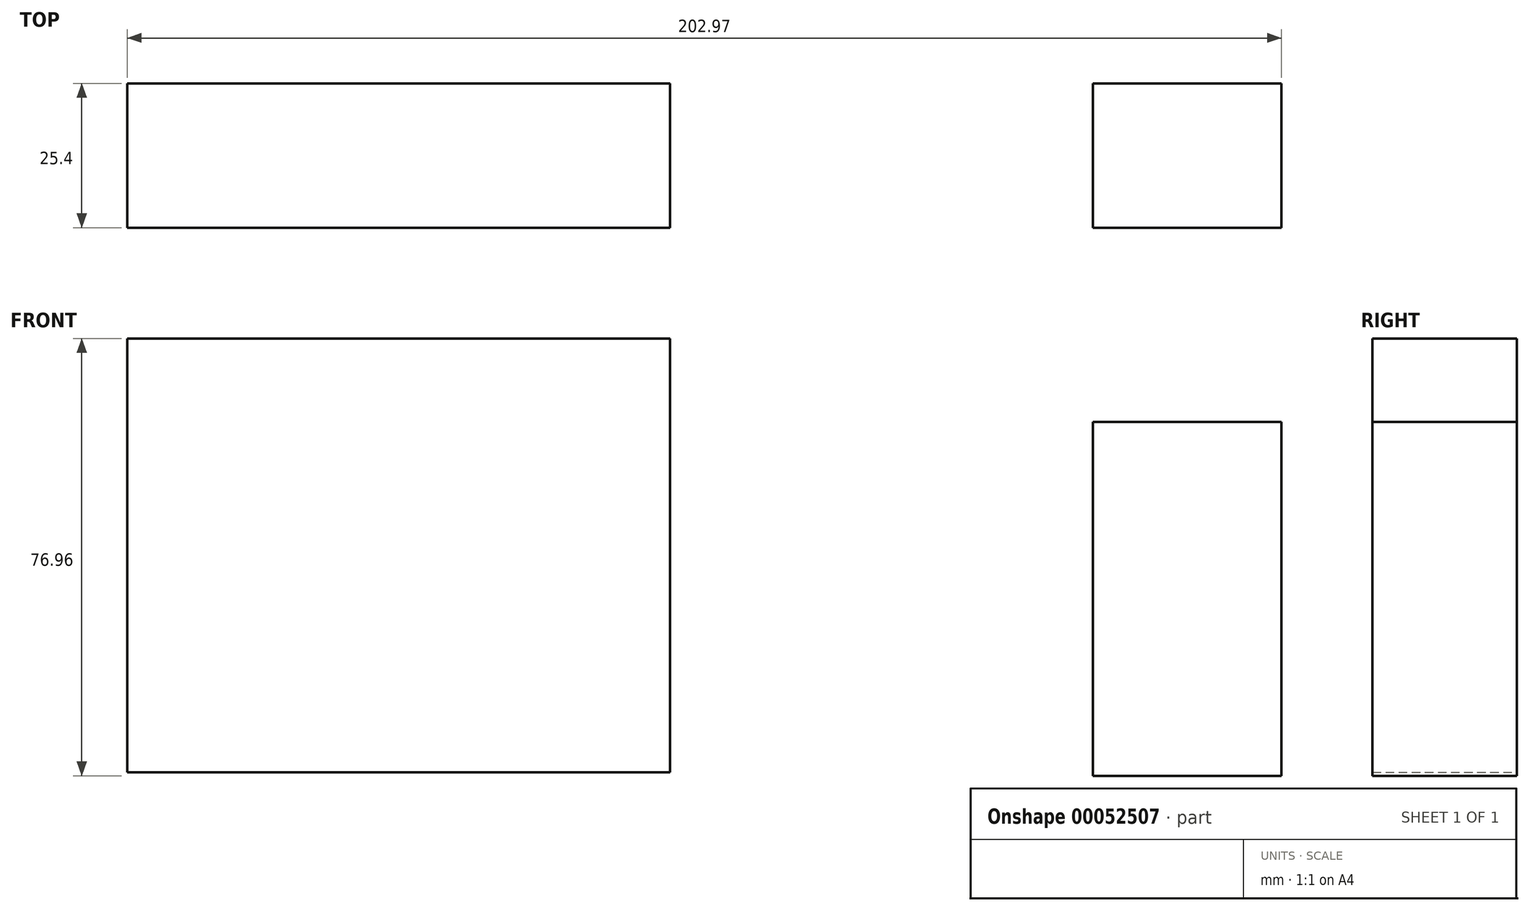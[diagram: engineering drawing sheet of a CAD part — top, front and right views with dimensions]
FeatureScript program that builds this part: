
annotation { "Feature Type Name" : "Feature", "Feature Type Description" : "" }
export const myFeature = defineFeature(function(context is Context, id is Id, definition is map)
    precondition{}
    {
        {
            var Q0;
            Q0=qCreatedBy(makeId("Front.planeOp"),FACE);
            var sketch = newSketch(context, id + "F0", { "sketchPlane" : qUnion([Q0])});
            skLineSegment(sketch, "E0.bottom", {"start": v(-122.85, 49.07) * mm, "end": v(-27.44, 49.07) * mm});
            skLineSegment(sketch, "E0.top", {"start": v(-122.85, -27.26) * mm, "end": v(-27.44, -27.26) * mm});
            skLineSegment(sketch, "E0.left", {"start": v(-122.85, 49.07) * mm, "end": v(-122.85, -27.26) * mm});
            skLineSegment(sketch, "E0.right", {"start": v(-27.44, 49.07) * mm, "end": v(-27.44, -27.26) * mm});
            skLineSegment(sketch, "E1.bottom", {"start": v(46.97, 34.37) * mm, "end": v(80.12, 34.37) * mm});
            skLineSegment(sketch, "E1.top", {"start": v(46.97, -27.9) * mm, "end": v(80.12, -27.9) * mm});
            skLineSegment(sketch, "E1.left", {"start": v(46.97, 34.37) * mm, "end": v(46.97, -27.9) * mm});
            skLineSegment(sketch, "E1.right", {"start": v(80.12, 34.37) * mm, "end": v(80.12, -27.9) * mm});
            skSolve(sketch);
        }
        {
            var Q0;
            Q0 = qSketchRegion(id + "F0", true);
            extrude(context, id + "F1", {"entities" : qUnion([Q0]), "depth" : 25.4 * mm});
        }
    });
